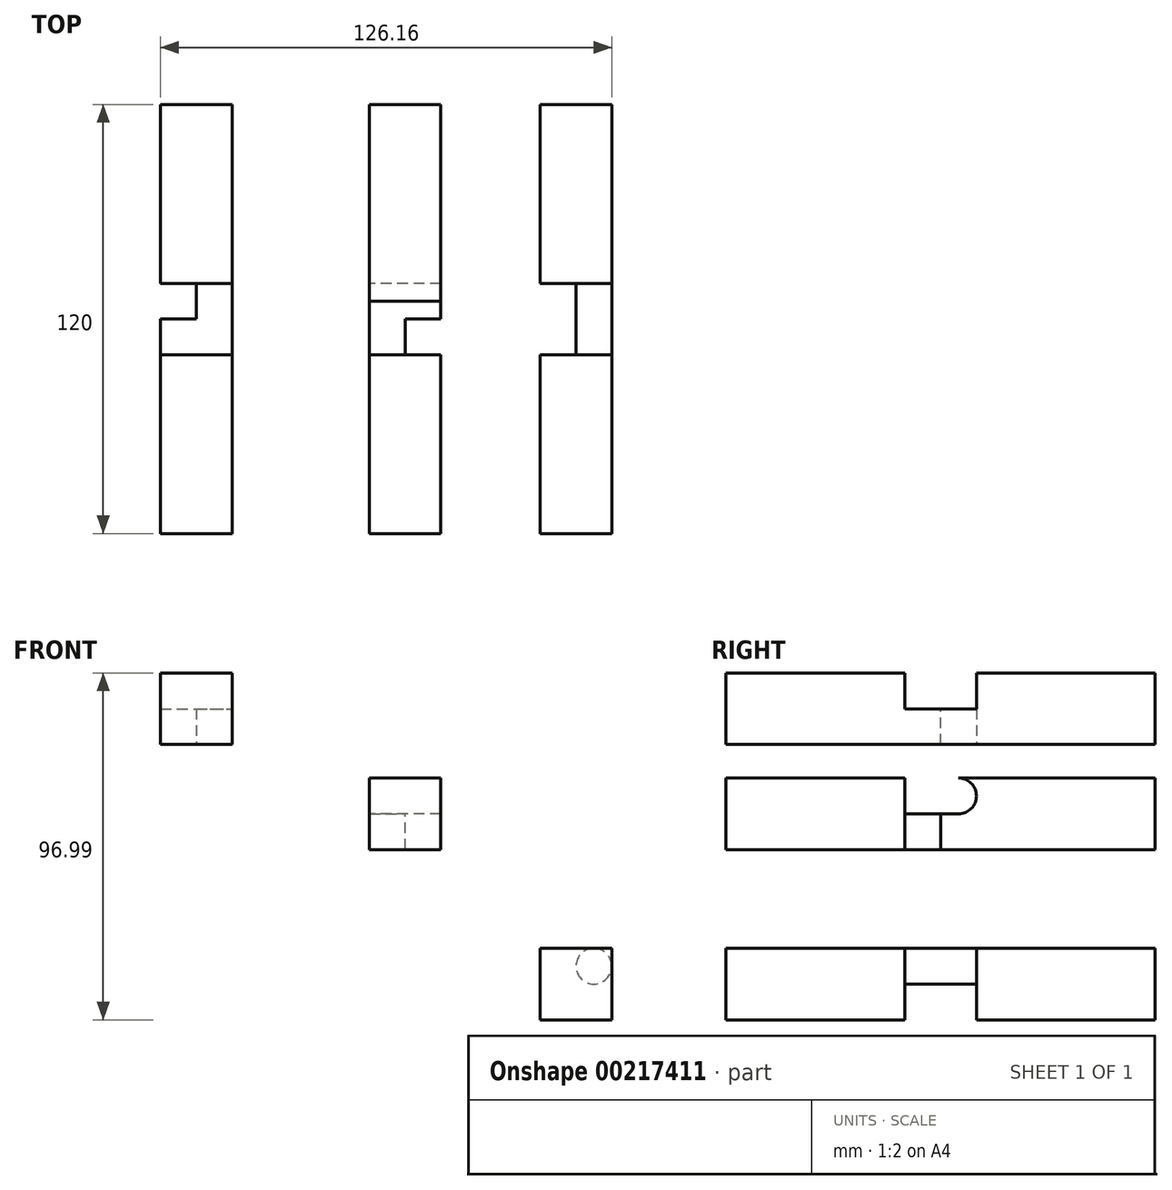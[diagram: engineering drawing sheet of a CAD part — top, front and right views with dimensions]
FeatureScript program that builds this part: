
annotation { "Feature Type Name" : "Feature", "Feature Type Description" : "" }
export const myFeature = defineFeature(function(context is Context, id is Id, definition is map)
    precondition{}
    {
        {
            var Q0;
            Q0=qCreatedBy(makeId("Front.planeOp"),FACE);
            var sketch = newSketch(context, id + "F0", { "sketchPlane" : qUnion([Q0])});
            skLineSegment(sketch, "E0.bottom", {"start": v(-67, 49.37) * mm, "end": v(-47, 49.37) * mm});
            skLineSegment(sketch, "E0.top", {"start": v(-67, 29.37) * mm, "end": v(-47, 29.37) * mm});
            skLineSegment(sketch, "E0.left", {"start": v(-67, 49.37) * mm, "end": v(-67, 29.37) * mm});
            skLineSegment(sketch, "E0.right", {"start": v(-47, 49.37) * mm, "end": v(-47, 29.37) * mm});
            skSolve(sketch);
        }
        {
            var Q0;
            Q0=makeQuery(id+"F0.imprint","IMPRINT",FACE,{"disambiguationData":[TD([[makeQuery(id+"F0.imprint","IMPRINT",EDGE,{"derivedFrom":sQuery(id+"F0.wireOp",EDGE,"E0.bottom")}),-1.0]])]});
            extrude(context, id + "F1", {"entities" : qUnion([Q0]), "depth" : 50 * mm});
        }
        {
            var Q0;
            Q0=makeQuery(id+"F1.opExtrude","CAP_FACE",FACE,{"disambiguationData":[OSD([sQuery(id+"F0.wireOp",EDGE,"E0.bottom"),sQuery(id+"F0.wireOp",EDGE,"E0.top"),sQuery(id+"F0.wireOp",EDGE,"E0.left"),sQuery(id+"F0.wireOp",EDGE,"E0.right")])],"isStart":false});
            var sketch = newSketch(context, id + "F2", { "sketchPlane" : qUnion([Q0])});
            skLineSegment(sketch, "E1.bottom", {"start": v(-67, 29.37) * mm, "end": v(-47, 29.37) * mm});
            skLineSegment(sketch, "E1.top", {"start": v(-67, 39.37) * mm, "end": v(-47, 39.37) * mm});
            skLineSegment(sketch, "E1.left", {"start": v(-67, 29.37) * mm, "end": v(-67, 39.37) * mm});
            skLineSegment(sketch, "E1.right", {"start": v(-47, 29.37) * mm, "end": v(-47, 39.37) * mm});
            skSolve(sketch);
        }
        {
            var Q0;
            Q0=makeQuery(id+"F2.imprint","IMPRINT",FACE,{"disambiguationData":[TD([[makeQuery(id+"F2.imprint","IMPRINT",EDGE,{"derivedFrom":sQuery(id+"F2.wireOp",EDGE,"E1.bottom")}),1.0]])]});
            extrude(context, id + "F3", {"entities" : qUnion([Q0]), "operationType" : NewBodyOperationType.ADD, "depth" : 10 * mm});
        }
        {
            var Q0;
            Q0=makeQuery(id+"F3.opExtrude","CAP_FACE",FACE,{"disambiguationData":[OSD([sQuery(id+"F2.wireOp",EDGE,"E1.bottom"),sQuery(id+"F2.wireOp",EDGE,"E1.top"),sQuery(id+"F2.wireOp",EDGE,"E1.left"),sQuery(id+"F2.wireOp",EDGE,"E1.right")])],"isStart":false});
            var sketch = newSketch(context, id + "F4", { "sketchPlane" : qUnion([Q0])});
            skLineSegment(sketch, "E2.bottom", {"start": v(-47, 39.37) * mm, "end": v(-57, 39.37) * mm});
            skLineSegment(sketch, "E2.top", {"start": v(-47, 29.37) * mm, "end": v(-57, 29.37) * mm});
            skLineSegment(sketch, "E2.left", {"start": v(-47, 39.37) * mm, "end": v(-47, 29.37) * mm});
            skLineSegment(sketch, "E2.right", {"start": v(-57, 39.37) * mm, "end": v(-57, 29.37) * mm});
            skSolve(sketch);
        }
        {
            var Q0;
            Q0=makeQuery(id+"F4.imprint","IMPRINT",FACE,{"disambiguationData":[TD([[makeQuery(id+"F4.imprint","IMPRINT",EDGE,{"derivedFrom":sQuery(id+"F4.wireOp",EDGE,"E2.bottom")}),-1.0]])]});
            extrude(context, id + "F5", {"entities" : qUnion([Q0]), "operationType" : NewBodyOperationType.ADD, "depth" : 10 * mm});
        }
        {
            var Q0;
            Q0=makeQuery(id+"F5.opExtrude","CAP_FACE",FACE,{"disambiguationData":[OSD([sQuery(id+"F4.wireOp",EDGE,"E2.bottom"),sQuery(id+"F4.wireOp",EDGE,"E2.top"),sQuery(id+"F4.wireOp",EDGE,"E2.left"),sQuery(id+"F4.wireOp",EDGE,"E2.right")])],"isStart":false});
            var sketch = newSketch(context, id + "F6", { "sketchPlane" : qUnion([Q0])});
            skLineSegment(sketch, "E3.bottom", {"start": v(-47, 29.37) * mm, "end": v(-67, 29.37) * mm});
            skLineSegment(sketch, "E3.top", {"start": v(-47, 49.37) * mm, "end": v(-67, 49.37) * mm});
            skLineSegment(sketch, "E3.left", {"start": v(-47, 29.37) * mm, "end": v(-47, 49.37) * mm});
            skLineSegment(sketch, "E3.right", {"start": v(-67, 29.37) * mm, "end": v(-67, 49.37) * mm});
            skSolve(sketch);
        }
        {
            var Q0;
            {var subQ2=sQuery(id+"F6.wireOp",EDGE,"E3.top");Q0=makeQuery(id+"F6.imprint","IMPRINT",FACE,{"disambiguationData":[TD([[makeQuery(id+"F6.imprint","IMPRINT",EDGE,{"derivedFrom":subQ2}),1.0]])]});}
            var Q1;
            {var subQ4=makeQuery(id+"F5.opExtrude","CAP_EDGE",EDGE,{"disambiguationData":[OSD([sQuery(id+"F4.wireOp",EDGE,"E2.bottom")])],"isStart":false});Q1=makeQuery(id+"F6.imprint","IMPRINT",FACE,{"disambiguationData":[TD([[makeQuery(id+"F6.imprint","IMPRINT",EDGE,{"derivedFrom":subQ4}),-1.0]])]});}
            extrude(context, id + "F7", {"entities" : qUnion([Q0, Q1]), "operationType" : NewBodyOperationType.ADD, "depth" : 50 * mm});
        }
        {
            var Q0;
            Q0=qCreatedBy(makeId("Front.planeOp"),FACE);
            var sketch = newSketch(context, id + "F8", { "sketchPlane" : qUnion([Q0])});
            skLineSegment(sketch, "E4.bottom", {"start": v(-8.6, 20) * mm, "end": v(11.4, 20) * mm});
            skLineSegment(sketch, "E4.top", {"start": v(-8.6, 0) * mm, "end": v(11.4, 0) * mm});
            skLineSegment(sketch, "E4.left", {"start": v(-8.6, 20) * mm, "end": v(-8.6, 0) * mm});
            skLineSegment(sketch, "E4.right", {"start": v(11.4, 20) * mm, "end": v(11.4, 0) * mm});
            skSolve(sketch);
        }
        {
            var Q0;
            Q0=makeQuery(id+"F8.imprint","IMPRINT",FACE,{"disambiguationData":[TD([[makeQuery(id+"F8.imprint","IMPRINT",EDGE,{"derivedFrom":sQuery(id+"F8.wireOp",EDGE,"E4.bottom")}),-1.0]])]});
            extrude(context, id + "F9", {"entities" : qUnion([Q0]), "depth" : 60 * mm});
        }
        {
            var Q0;
            Q0=makeQuery(id+"F9.opExtrude","CAP_FACE",FACE,{"disambiguationData":[OSD([sQuery(id+"F8.wireOp",EDGE,"E4.bottom"),sQuery(id+"F8.wireOp",EDGE,"E4.top"),sQuery(id+"F8.wireOp",EDGE,"E4.left"),sQuery(id+"F8.wireOp",EDGE,"E4.right")])],"isStart":false});
            var sketch = newSketch(context, id + "F10", { "sketchPlane" : qUnion([Q0])});
            skLineSegment(sketch, "E5.bottom", {"start": v(-8.6, 0) * mm, "end": v(1.4, 0) * mm});
            skLineSegment(sketch, "E5.top", {"start": v(-8.6, 10) * mm, "end": v(1.4, 10) * mm});
            skLineSegment(sketch, "E5.left", {"start": v(-8.6, 0) * mm, "end": v(-8.6, 10) * mm});
            skLineSegment(sketch, "E5.right", {"start": v(1.4, 0) * mm, "end": v(1.4, 10) * mm});
            skSolve(sketch);
        }
        {
            var Q0;
            Q0=makeQuery(id+"F10.imprint","IMPRINT",FACE,{"disambiguationData":[TD([[makeQuery(id+"F10.imprint","IMPRINT",EDGE,{"derivedFrom":sQuery(id+"F10.wireOp",EDGE,"E5.bottom")}),1.0]])]});
            extrude(context, id + "F11", {"entities" : qUnion([Q0]), "operationType" : NewBodyOperationType.ADD, "depth" : 10 * mm});
        }
        {
            var Q0;
            Q0=makeQuery(id+"F11.boolean.opBoolean","MERGE",FACE,{"derivedFrom":[makeQuery(id+"F9.opExtrude","SWEPT_FACE",FACE,{"disambiguationData":[OSD([sQuery(id+"F8.wireOp",EDGE,"E4.left")])]}),makeQuery(id+"F11.opExtrude","SWEPT_FACE",FACE,{"disambiguationData":[OSD([sQuery(id+"F10.wireOp",EDGE,"E5.left")])]})]});
            var sketch = newSketch(context, id + "F12", { "sketchPlane" : qUnion([Q0])});
            skArc(sketch, "E6", {"start": v(55, 20) * mm, "mid": v(50, 15) * mm, "end": v(55, 10) * mm});
            skLineSegment(sketch, "E7", {"start": v(55, 10) * mm, "end": v(60, 10) * mm});
            skLineSegment(sketch, "E8", {"start": v(55, 20) * mm, "end": v(60, 20) * mm});
            skSolve(sketch);
        }
        {
            var Q0;
            Q0=makeQuery(id+"F12.imprint","IMPRINT",FACE,{"disambiguationData":[TD([[makeQuery(id+"F12.imprint","IMPRINT",EDGE,{"derivedFrom":sQuery(id+"F12.wireOp",EDGE,"E6")}),1.0]])]});
            extrude(context, id + "F13", {"entities" : qUnion([Q0]), "operationType" : NewBodyOperationType.REMOVE, "oppositeDirection" : true, "depth" : 20 * mm});
        }
        {
            var Q0;
            Q0=makeQuery(id+"F11.opExtrude","CAP_FACE",FACE,{"disambiguationData":[OSD([sQuery(id+"F10.wireOp",EDGE,"E5.bottom"),sQuery(id+"F10.wireOp",EDGE,"E5.top"),sQuery(id+"F10.wireOp",EDGE,"E5.left"),sQuery(id+"F10.wireOp",EDGE,"E5.right")])],"isStart":false});
            var sketch = newSketch(context, id + "F14", { "sketchPlane" : qUnion([Q0])});
            skLineSegment(sketch, "E9.bottom", {"start": v(-8.6, 0) * mm, "end": v(11.4, 0) * mm});
            skLineSegment(sketch, "E9.top", {"start": v(-8.6, 20) * mm, "end": v(11.4, 20) * mm});
            skLineSegment(sketch, "E9.left", {"start": v(-8.6, 0) * mm, "end": v(-8.6, 20) * mm});
            skLineSegment(sketch, "E9.right", {"start": v(11.4, 0) * mm, "end": v(11.4, 20) * mm});
            skSolve(sketch);
        }
        {
            var Q0;
            {var subQ4=makeQuery(id+"F11.opExtrude","CAP_EDGE",EDGE,{"disambiguationData":[OSD([sQuery(id+"F10.wireOp",EDGE,"E5.top")])],"isStart":false});Q0=makeQuery(id+"F14.imprint","IMPRINT",FACE,{"disambiguationData":[TD([[makeQuery(id+"F14.imprint","IMPRINT",EDGE,{"derivedFrom":subQ4}),-1.0]])]});}
            var Q1;
            {var subQ2=sQuery(id+"F14.wireOp",EDGE,"E9.top");Q1=makeQuery(id+"F14.imprint","IMPRINT",FACE,{"disambiguationData":[TD([[makeQuery(id+"F14.imprint","IMPRINT",EDGE,{"derivedFrom":subQ2}),-1.0]])]});}
            extrude(context, id + "F15", {"entities" : qUnion([Q0, Q1]), "operationType" : NewBodyOperationType.ADD, "depth" : 50 * mm});
        }
        {
            var Q0;
            Q0=qCreatedBy(makeId("Front.planeOp"),FACE);
            var sketch = newSketch(context, id + "F16", { "sketchPlane" : qUnion([Q0])});
            skLineSegment(sketch, "E10.bottom", {"start": v(39.15, -27.62) * mm, "end": v(59.15, -27.62) * mm});
            skLineSegment(sketch, "E10.top", {"start": v(39.15, -47.62) * mm, "end": v(59.15, -47.62) * mm});
            skLineSegment(sketch, "E10.left", {"start": v(39.15, -27.62) * mm, "end": v(39.15, -47.62) * mm});
            skLineSegment(sketch, "E10.right", {"start": v(59.15, -27.62) * mm, "end": v(59.15, -47.62) * mm});
            skSolve(sketch);
        }
        {
            var Q0;
            Q0=makeQuery(id+"F16.imprint","IMPRINT",FACE,{"disambiguationData":[TD([[makeQuery(id+"F16.imprint","IMPRINT",EDGE,{"derivedFrom":sQuery(id+"F16.wireOp",EDGE,"E10.bottom")}),-1.0]])]});
            extrude(context, id + "F17", {"entities" : qUnion([Q0]), "depth" : 50 * mm});
        }
        {
            var Q0;
            Q0=makeQuery(id+"F17.opExtrude","CAP_FACE",FACE,{"disambiguationData":[OSD([sQuery(id+"F16.wireOp",EDGE,"E10.bottom"),sQuery(id+"F16.wireOp",EDGE,"E10.top"),sQuery(id+"F16.wireOp",EDGE,"E10.left"),sQuery(id+"F16.wireOp",EDGE,"E10.right")])],"isStart":false});
            var sketch = newSketch(context, id + "F18", { "sketchPlane" : qUnion([Q0])});
            skCircle(sketch, "E11", {"center": v(54.15, -32.62) * mm, "radius": 5 * mm});
            skSolve(sketch);
        }
        {
            var Q0;
            {var subQ0=sQuery(id+"F18.wireOp",EDGE,"E11");var subQ1=makeQuery(id+"F18.imprint","INTERSECT",VERTEX,{"derivedFrom":[makeQuery(id+"F17.opExtrude","CAP_EDGE",EDGE,{"disambiguationData":[OSD([sQuery(id+"F16.wireOp",EDGE,"E10.bottom")])],"isStart":false}),subQ0]});Q0=makeQuery(id+"F18.imprint","IMPRINT",FACE,{"disambiguationData":[TD([[makeQuery(id+"F18.imprint","IMPRINT",EDGE,{"disambiguationData":[TD([[subQ1,1.0]])],"derivedFrom":subQ0}),1.0]])]});}
            extrude(context, id + "F19", {"entities" : qUnion([Q0]), "operationType" : NewBodyOperationType.ADD, "depth" : 20 * mm});
        }
        {
            var Q0;
            Q0=makeQuery(id+"F19.opExtrude","CAP_FACE",FACE,{"disambiguationData":[OSD([sQuery(id+"F18.wireOp",EDGE,"E11")])],"isStart":false});
            var sketch = newSketch(context, id + "F20", { "sketchPlane" : qUnion([Q0])});
            skLineSegment(sketch, "E12.bottom", {"start": v(39.15, -27.62) * mm, "end": v(59.15, -27.62) * mm});
            skLineSegment(sketch, "E12.top", {"start": v(39.15, -47.62) * mm, "end": v(59.15, -47.62) * mm});
            skLineSegment(sketch, "E12.left", {"start": v(39.15, -27.62) * mm, "end": v(39.15, -47.62) * mm});
            skLineSegment(sketch, "E12.right", {"start": v(59.15, -27.62) * mm, "end": v(59.15, -47.62) * mm});
            skSolve(sketch);
        }
        {
            var Q0;
            {var subQ1=sQuery(id+"F20.wireOp",EDGE,"E12.top");Q0=makeQuery(id+"F20.imprint","IMPRINT",FACE,{"disambiguationData":[TD([[makeQuery(id+"F20.imprint","IMPRINT",EDGE,{"derivedFrom":subQ1}),1.0]])]});}
            var Q1;
            {var subQ0=makeQuery(id+"F19.opExtrude","CAP_EDGE",EDGE,{"disambiguationData":[OSD([sQuery(id+"F18.wireOp",EDGE,"E11")])],"isStart":false});var subQ1=makeQuery(id+"F20.imprint","INTERSECT",VERTEX,{"derivedFrom":[subQ0,sQuery(id+"F20.wireOp",EDGE,"E12.bottom")]});Q1=makeQuery(id+"F20.imprint","IMPRINT",FACE,{"disambiguationData":[TD([[makeQuery(id+"F20.imprint","IMPRINT",EDGE,{"disambiguationData":[TD([[subQ1,-1.0]])],"derivedFrom":subQ0}),1.0]])]});}
            var Q2;
            {var subQ0=sQuery(id+"F20.wireOp",EDGE,"E12.right");var subQ1=sQuery(id+"F20.wireOp",EDGE,"E12.bottom");var subQ2=makeQuery(id+"F20.imprint","INTERSECT",VERTEX,{"derivedFrom":[subQ1,subQ0]});Q2=makeQuery(id+"F20.imprint","IMPRINT",FACE,{"disambiguationData":[TD([[makeQuery(id+"F20.imprint","IMPRINT",EDGE,{"disambiguationData":[TD([[subQ2,1.0]])],"derivedFrom":subQ1}),-1.0]])]});}
            extrude(context, id + "F21", {"entities" : qUnion([Q0, Q1, Q2]), "operationType" : NewBodyOperationType.ADD, "depth" : 50 * mm});
        }
        {
            var Q0;
            Q0=makeQuery(id+"F3.opExtrude","CAP_FACE",FACE,{"disambiguationData":[OSD([sQuery(id+"F2.wireOp",EDGE,"E1.bottom"),sQuery(id+"F2.wireOp",EDGE,"E1.top"),sQuery(id+"F2.wireOp",EDGE,"E1.left"),sQuery(id+"F2.wireOp",EDGE,"E1.right")])],"isStart":false});
            extrude(context, id + "F22", {"entities" : qUnion([Q0]), "operationType" : NewBodyOperationType.REMOVE, "oppositeDirection" : true, "depth" : 10 * mm});
        }
        {
            var Q0;
            {var subQ0=sQuery(id+"F4.wireOp",EDGE,"E2.right");Q0=makeQuery(id+"F22.boolean.opBoolean","MERGE",FACE,{"derivedFrom":[makeQuery(id+"F5.opExtrude","SWEPT_FACE",FACE,{"disambiguationData":[OSD([subQ0])]}),makeQuery(id+"F22.opExtrude","SWEPT_FACE",FACE,{"disambiguationData":[OSD([subQ0])]})]});}
            var sketch = newSketch(context, id + "F23", { "sketchPlane" : qUnion([Q0])});
            skLineSegment(sketch, "E13.bottom", {"start": v(70, 29.37) * mm, "end": v(60, 29.37) * mm});
            skLineSegment(sketch, "E13.top", {"start": v(70, 39.37) * mm, "end": v(60, 39.37) * mm});
            skLineSegment(sketch, "E13.left", {"start": v(70, 29.37) * mm, "end": v(70, 39.37) * mm});
            skLineSegment(sketch, "E13.right", {"start": v(60, 29.37) * mm, "end": v(60, 39.37) * mm});
            skSolve(sketch);
        }
        {
            var Q0;
            Q0=makeQuery(id+"F23.imprint","IMPRINT",FACE,{"disambiguationData":[TD([[makeQuery(id+"F23.imprint","IMPRINT",EDGE,{"derivedFrom":sQuery(id+"F23.wireOp",EDGE,"E13.bottom")}),-1.0]])]});
            extrude(context, id + "F24", {"entities" : qUnion([Q0]), "operationType" : NewBodyOperationType.ADD, "depth" : 10 * mm});
        }
    });
